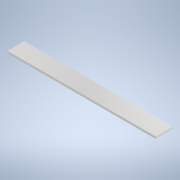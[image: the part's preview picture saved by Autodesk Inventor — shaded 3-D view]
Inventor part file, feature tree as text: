
AUTODESK INVENTOR PART (.ipt)
format: ipt  version: 2022 (Build 260153000, 153)  size: 103,936 bytes
history: native  units: mm
features: other x1, extrude x1, sketch x1
ambient origin geometry x8: Origin, YZ Plane, XZ Plane, XY Plane, X Axis, Y Axis, Z Axis, Center Point
bodies: Body1 (feature_tree)
feature tree (3):
  other  "ソリッド1"
  extrude  "押し出し1"  Depth=40.0mm
  sketch  "スケッチ1"
